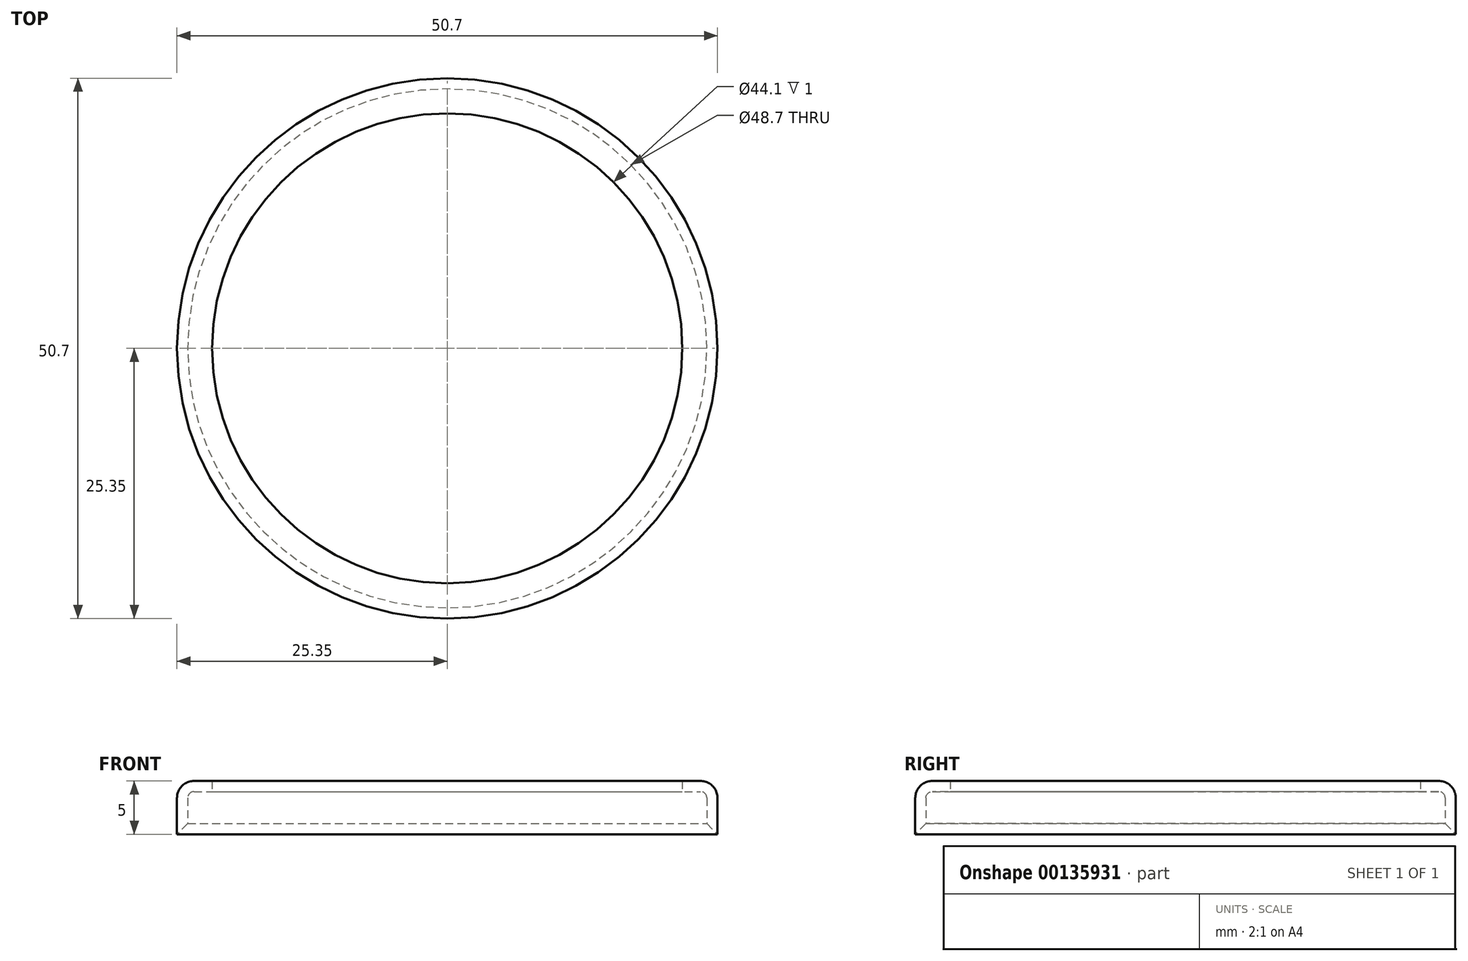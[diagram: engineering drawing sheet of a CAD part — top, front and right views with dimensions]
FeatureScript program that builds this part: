
annotation { "Feature Type Name" : "Feature", "Feature Type Description" : "" }
export const myFeature = defineFeature(function(context is Context, id is Id, definition is map)
    precondition{}
    {
        {
            var Q0;
            Q0=qCreatedBy(makeId("Front.planeOp"),FACE);
            var sketch = newSketch(context, id + "F0", { "sketchPlane" : qUnion([Q0])});
            skLineSegment(sketch, "E0", {"start": v(0, 0) * mm, "end": v(0, 36.8) * mm, "construction": true});
            skSolve(sketch);
        }
        {
            var Q0;
            Q0=qCreatedBy(makeId("Front.planeOp"),FACE);
            var sketch = newSketch(context, id + "F1", { "sketchPlane" : qUnion([Q0])});
            skLineSegment(sketch, "E1", {"start": v(-25.35, 0) * mm, "end": v(-25.35, 3.4) * mm});
            skArc(sketch, "E2", {"start": v(-23.75, 5) * mm, "mid": v(-24.88, 4.53) * mm, "end": v(-25.35, 3.4) * mm});
            skArc(sketch, "E3", {"start": v(-23.75, 4) * mm, "mid": v(-24.17, 3.83) * mm, "end": v(-24.35, 3.4) * mm});
            skLineSegment(sketch, "E4", {"start": v(-23.75, 4) * mm, "end": v(-22.05, 4) * mm});
            skLineSegment(sketch, "E5", {"start": v(-22.05, 4) * mm, "end": v(-22.05, 5) * mm});
            skLineSegment(sketch, "E6", {"start": v(-22.05, 5) * mm, "end": v(-23.75, 5) * mm});
            skLineSegment(sketch, "E7", {"start": v(-25.35, 0) * mm, "end": v(-24.35, 1) * mm});
            skLineSegment(sketch, "E8", {"start": v(-24.35, 1) * mm, "end": v(-24.35, 3.4) * mm});
            skSolve(sketch);
        }
        {
            var Q0;
            Q0 = qSketchRegion(id + "F1", true);
            var Q1;
            Q1=sQuery(id+"F0.wireOp",EDGE,"E0");
            revolve(context, id + "F2", {"entities" : qUnion([Q0]), "axis" : qUnion([Q1]), "revolveType" : RevolveType.FULL});
        }
    });
